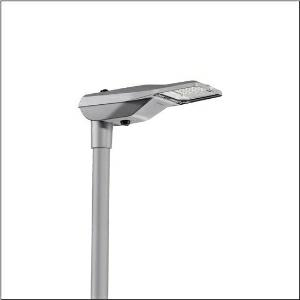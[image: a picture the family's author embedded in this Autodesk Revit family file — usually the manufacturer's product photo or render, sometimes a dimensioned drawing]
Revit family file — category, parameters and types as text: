
# Revit family: streetlight_sl_21_iq_micro___st1_0a_5xe1d41y08cb_9909
name_source: partatom
category: Lighting Fixtures
units: mm (PartAtom-declared; Revit-internal decimal feet)

## family parameters
Cut with Voids When Loaded = No
Host = Face
Light Source = No
Part Type = Normal
Room Calculation Point = No
Round Connector Dimension = Use Diameter
Shared = No

## types (1)
- --- (1 x LED, 2970 lm, 19.1 W, 4000K)
    Apparent Load = 19 VA
    CIE Flux Codes = 37 72 97 100 100
    Color Rendering = 70
    Color Temperature = 4000K
    Default Elevation = 1800 mm
    Description = Streetlight SL 21 iQ micro, mast luminaire, primary light control with lens, of PMMA, primary optical cover: cover, of toughened safety glass, transparent, light distribution: ST1.0a, light emission: direct distribution, primary light characteristic: asymmetric, installation type: post-top, side-entry, LED, High Power LED, rated luminous flux: 2.970lm, luminous efficacy: 156lm/W, light colour: 740, colour temperature: 4000K, control gear: iQ-Street Remote, D4i with power reduction, control: pre-setting: logarithmic dimming characteristic, Street-Remote, Auto-Match, Temp-Guard, Lumen-Switch, Night-Set, Smart-Wire, Light-Fading, Desk-Remote (wireless, voltage-free reading and setting of iQ features in the workshop via application-optimized NFC function/RFID function), optimised constant luminous flux control (CLO 2.0), mains connection: 220..240V, AC, 50/60Hz, start of lifetime: 19W, end of service life: 20W, reduction: 9W, luminaire housing, of diecast aluminium, powder-coated, SITECO metallic grey (DB 702S), corrosivity category C5 high according to DIN EN ISO 12944, please order mast flange separately, inclination adjustable: 0°, 5°, 10°, 15°, sealing non-destructively replaceable, multi-level sealing system, length: 528mm, width: 235mm, height: 110mm, mast flange for spigot size: 42mm (side-entry): 5XC10008XM4, 60/48mm (side-entry/post-top): 5XC10108XM2, 76/60mm (side-entry/post-top): 5XC10108XM1, mounting height: 4..8m, Smart Interface below and above, protection rating (complete): IP66, insulation class (complete): insulation class II (safety insulation), certification: CE, ENEC, ENEC+, VDE, impact resistance: IK10, permissible operating ambient temperature for outdoor applications: -40..+50°C, standard-compliant lighting for roads and squares, packaging unit: 1 piece

Light Distribution: ST1.0a
    Height = 110 mm
    Lamp = 1 x LED
    Lamp Light Flux = 2970 lm
    Lamp Power = 19.1 W
    Lamp count = 1
    Length = 528 mm
    Luminous efficacy = 156 lm/W
    Manufacturer = Siteco
    ModVariant = No
    Model = 5XE1D41Y08CB
    Number of Poles = 1
    OnlyDefault = Yes
    Power Factor = 1
    Product Name = Streetlight SL 21 iQ micro | ST1.0a
    Product group = mast luminaire | pylon top
    ProductGroupID = 6100
    Protection Class = Protection class II
    Protection Degree = IP 66
    RLX_Detail_Level = 1
    RLX_Emergency_Light_Flux = 0 lm
    RLX_Emergency_Type = 0
    RLX_Emergency_Type_DB = No
    RlxData = <blob elided: 98789 chars, md5=263e6f39>
    Socket = socket
    Standby Power = 0 W
    System Light Flux = 2970 lm
    System Power = 19 W
    Type Comments = factory setting: luminous flux: 100 % | dim-lin: 254 | 387 mA
    Type Image = l_1007239.jpg
    URL = http://relux.com
    VarID = @adj_115427
    Voltage = 0 V
    Weight = 0.00 kg
    Width = 235 mm

## geometry (parser evidence)
native form markers: Blend x4, Sweep x12
no freeform markers — native parametric forms only
